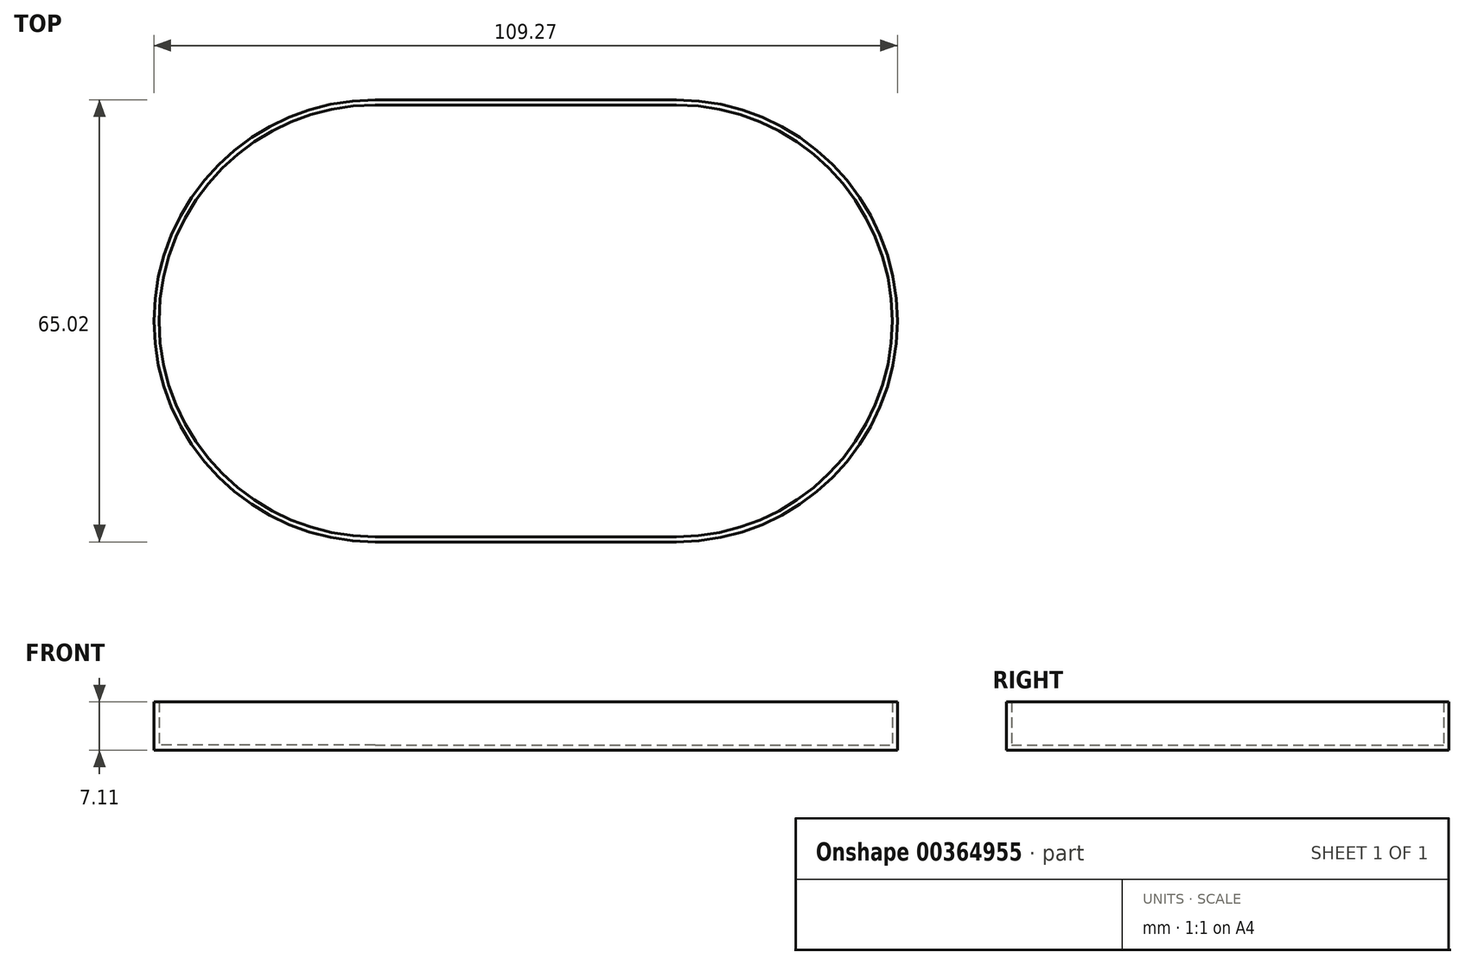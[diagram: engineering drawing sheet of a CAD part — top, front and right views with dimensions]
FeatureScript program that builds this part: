
annotation { "Feature Type Name" : "Feature", "Feature Type Description" : "" }
export const myFeature = defineFeature(function(context is Context, id is Id, definition is map)
    precondition{}
    {
        {
            var Q0;
            Q0=qCreatedBy(makeId("Top.planeOp"),FACE);
            var sketch = newSketch(context, id + "F0", { "sketchPlane" : qUnion([Q0])});
            skArc(sketch, "E0", {"start": v(0, -31.75) * mm, "mid": v(31.75, 0) * mm, "end": v(0, 31.75) * mm});
            skLineSegment(sketch, "E1", {"start": v(-44.25, 31.75) * mm, "end": v(0, 31.75) * mm});
            skLineSegment(sketch, "E2", {"start": v(-44.25, -31.75) * mm, "end": v(0, -31.75) * mm});
            skArc(sketch, "E3.trimOffspring", {"start": v(-44.25, 31.75) * mm, "mid": v(-76, 0) * mm, "end": v(-44.25, -31.75) * mm});
            skSolve(sketch);
        }
        {
            var Q0;
            Q0=makeQuery(id+"F0.imprint","IMPRINT",FACE,{"disambiguationData":[TD([[makeQuery(id+"F0.imprint","IMPRINT",EDGE,{"derivedFrom":sQuery(id+"F0.wireOp",EDGE,"E0")}),1.0]])]});
            extrude(context, id + "F1", {"entities" : qUnion([Q0]), "depth" : 6.35 * mm});
        }
        {
            var Q0;
            Q0=makeQuery(id+"F1.opExtrude","CAP_FACE",FACE,{"disambiguationData":[OSD([sQuery(id+"F0.wireOp",EDGE,"E0"),sQuery(id+"F0.wireOp",EDGE,"E1"),sQuery(id+"F0.wireOp",EDGE,"E2"),sQuery(id+"F0.wireOp",EDGE,"E3.trimOffspring")])],"isStart":false});
            shell(context, id + "F2", {"entities" : qUnion([Q0]), "thickness" : 0.76 * mm, "oppositeDirection" : true});
        }
    });
